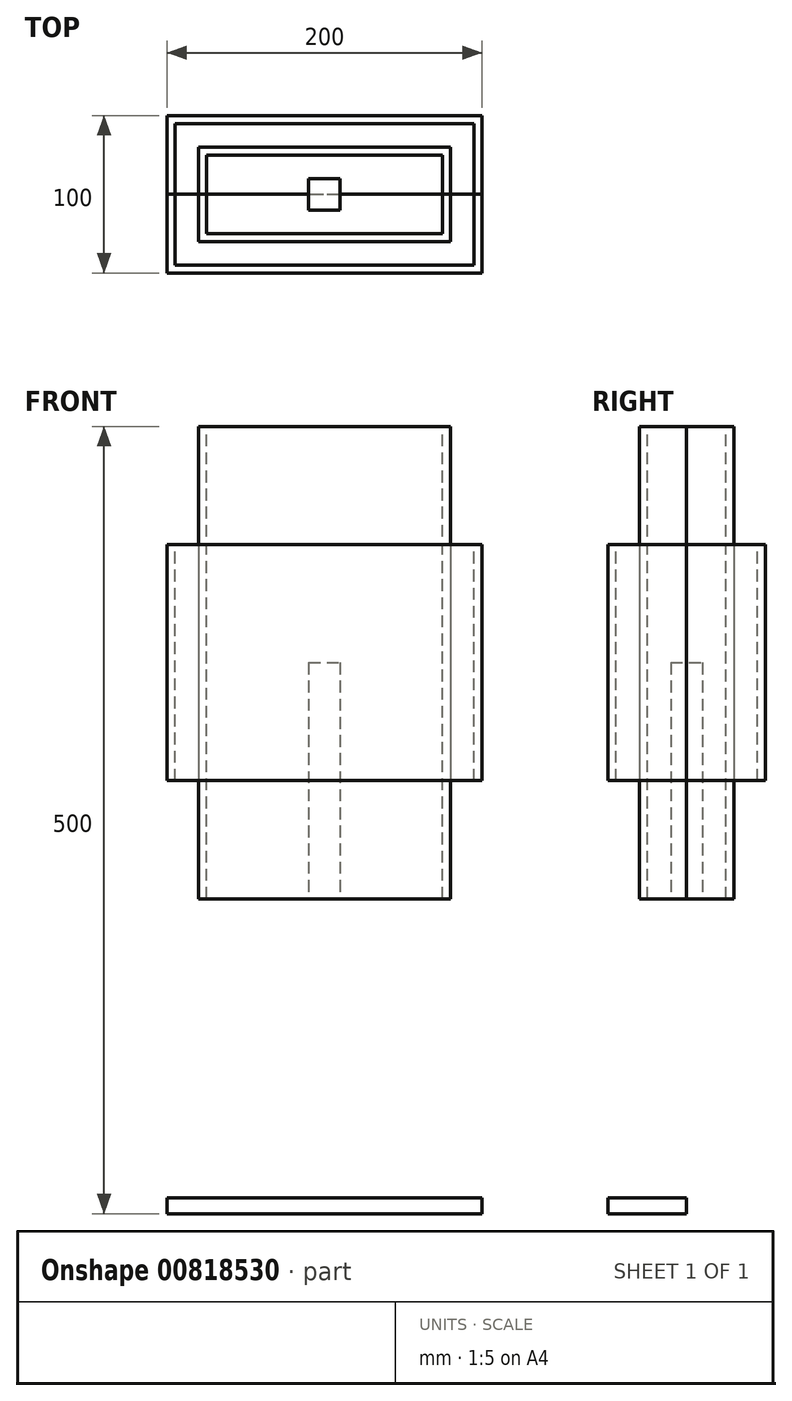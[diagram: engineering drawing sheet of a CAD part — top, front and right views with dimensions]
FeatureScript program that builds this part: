
annotation { "Feature Type Name" : "Feature", "Feature Type Description" : "" }
export const myFeature = defineFeature(function(context is Context, id is Id, definition is map)
    precondition{}
    {
        {
            var Q0;
            Q0=qCreatedBy(makeId("Front.planeOp"),FACE);
            var sketch = newSketch(context, id + "F0", { "sketchPlane" : qUnion([Q0])});
            skLineSegment(sketch, "E0.bottom", {"start": v(-100, 425) * mm, "end": v(100, 425) * mm});
            skLineSegment(sketch, "E0.top", {"start": v(-100, 275) * mm, "end": v(100, 275) * mm});
            skLineSegment(sketch, "E0.left", {"start": v(-100, 425) * mm, "end": v(-100, 275) * mm});
            skLineSegment(sketch, "E0.right", {"start": v(100, 425) * mm, "end": v(100, 275) * mm});
            skLineSegment(sketch, "E1.bottom", {"start": v(-95, 420) * mm, "end": v(95, 420) * mm});
            skLineSegment(sketch, "E1.top", {"start": v(-95, 280) * mm, "end": v(95, 280) * mm});
            skLineSegment(sketch, "E1.left", {"start": v(-95, 420) * mm, "end": v(-95, 280) * mm});
            skLineSegment(sketch, "E1.right", {"start": v(95, 420) * mm, "end": v(95, 280) * mm});
            skLineSegment(sketch, "E2", {"start": v(0, 425) * mm, "end": v(0, 420) * mm});
            skLineSegment(sketch, "E3", {"start": v(-95, 350) * mm, "end": v(-100, 350) * mm, "construction": true});
            skPoint(sketch, "E3.endSnap0", {"position": v(-100, 350) * mm});
            skLineSegment(sketch, "E4.bottom", {"start": v(-100, 10) * mm, "end": v(100, 10) * mm});
            skLineSegment(sketch, "E4.top", {"start": v(-100, 0) * mm, "end": v(100, 0) * mm});
            skLineSegment(sketch, "E4.left", {"start": v(-100, 10) * mm, "end": v(-100, 0) * mm});
            skLineSegment(sketch, "E4.right", {"start": v(100, 10) * mm, "end": v(100, 0) * mm});
            skLineSegment(sketch, "E5.bottom", {"start": v(-10, 350) * mm, "end": v(10, 350) * mm});
            skLineSegment(sketch, "E5.top", {"start": v(-10, 10) * mm, "end": v(10, 10) * mm});
            skLineSegment(sketch, "E5.left", {"start": v(-10, 350) * mm, "end": v(-10, 10) * mm});
            skLineSegment(sketch, "E5.right", {"start": v(10, 350) * mm, "end": v(10, 10) * mm});
            skLineSegment(sketch, "E6", {"start": v(0, 350) * mm, "end": v(0, 10) * mm, "construction": true});
            skLineSegment(sketch, "E7.bottom", {"start": v(-75, 495) * mm, "end": v(75, 495) * mm});
            skLineSegment(sketch, "E7.top", {"start": v(-75, 205) * mm, "end": v(75, 205) * mm});
            skLineSegment(sketch, "E7.left", {"start": v(-75, 495) * mm, "end": v(-75, 205) * mm});
            skLineSegment(sketch, "E7.right", {"start": v(75, 495) * mm, "end": v(75, 205) * mm});
            skLineSegment(sketch, "E8.bottom", {"start": v(-80, 500) * mm, "end": v(80, 500) * mm});
            skLineSegment(sketch, "E8.top", {"start": v(-80, 200) * mm, "end": v(80, 200) * mm});
            skLineSegment(sketch, "E8.left", {"start": v(-80, 500) * mm, "end": v(-80, 200) * mm});
            skLineSegment(sketch, "E8.right", {"start": v(80, 500) * mm, "end": v(80, 200) * mm});
            skLineSegment(sketch, "E9", {"start": v(0, 500) * mm, "end": v(0, 495) * mm, "construction": true});
            skLineSegment(sketch, "E10", {"start": v(-75, 350) * mm, "end": v(-80, 350) * mm, "construction": true});
            skLineSegment(sketch, "E11", {"start": v(0, 495) * mm, "end": v(0, 425) * mm, "construction": true});
            skLineSegment(sketch, "E12", {"start": v(0, 275) * mm, "end": v(0, 205) * mm, "construction": true});
            skLineSegment(sketch, "E13", {"start": v(-75, 350) * mm, "end": v(75, 350) * mm, "construction": true});
            skLineSegment(sketch, "E14", {"start": v(-75, 205) * mm, "end": v(-75, 200) * mm});
            skLineSegment(sketch, "E15", {"start": v(75, 205) * mm, "end": v(75, 200) * mm});
            skLineSegment(sketch, "E16", {"start": v(-95, 280) * mm, "end": v(-95, 275) * mm});
            skLineSegment(sketch, "E17", {"start": v(95, 280) * mm, "end": v(95, 275) * mm});
            skLineSegment(sketch, "E18", {"start": v(-75, 495) * mm, "end": v(-75, 500) * mm});
            skLineSegment(sketch, "E19", {"start": v(75, 495) * mm, "end": v(75, 500) * mm});
            skLineSegment(sketch, "E20", {"start": v(-95, 420) * mm, "end": v(-95, 425) * mm});
            skLineSegment(sketch, "E21", {"start": v(95, 420) * mm, "end": v(95, 425) * mm});
            skSolve(sketch);
        }
        {
            var Q0;
            {var subQ0=sQuery(id+"F0.wireOp",EDGE,"E5.top");Q0=makeQuery(id+"F0.imprint","IMPRINT",FACE,{"disambiguationData":[TD([[makeQuery(id+"F0.imprint","IMPRINT",EDGE,{"derivedFrom":subQ0}),1.0]])]});}
            var Q1;
            {var subQ0=sQuery(id+"F0.wireOp",EDGE,"E8.top");var subQ1=sQuery(id+"F0.wireOp",EDGE,"E5.left");var subQ2=makeQuery(id+"F0.imprint","INTERSECT",VERTEX,{"derivedFrom":[subQ1,subQ0]});Q1=makeQuery(id+"F0.imprint","IMPRINT",FACE,{"disambiguationData":[TD([[makeQuery(id+"F0.imprint","IMPRINT",EDGE,{"disambiguationData":[TD([[subQ2,1.0]])],"derivedFrom":subQ1}),1.0]])]});}
            var Q2;
            {var subQ0=sQuery(id+"F0.wireOp",EDGE,"E5.left");var subQ1=sQuery(id+"F0.wireOp",EDGE,"E0.top");var subQ2=makeQuery(id+"F0.imprint","INTERSECT",VERTEX,{"derivedFrom":[subQ1,subQ0]});Q2=makeQuery(id+"F0.imprint","IMPRINT",FACE,{"disambiguationData":[TD([[makeQuery(id+"F0.imprint","IMPRINT",EDGE,{"disambiguationData":[TD([[subQ2,-1.0]])],"derivedFrom":subQ1}),-1.0]])]});}
            var Q3;
            {var subQ0=sQuery(id+"F0.wireOp",EDGE,"E5.left");var subQ1=sQuery(id+"F0.wireOp",EDGE,"E0.top");var subQ2=makeQuery(id+"F0.imprint","INTERSECT",VERTEX,{"derivedFrom":[subQ1,subQ0]});Q3=makeQuery(id+"F0.imprint","IMPRINT",FACE,{"disambiguationData":[TD([[makeQuery(id+"F0.imprint","IMPRINT",EDGE,{"disambiguationData":[TD([[subQ2,-1.0]])],"derivedFrom":subQ1}),1.0]])]});}
            var Q4;
            {var subQ5=sQuery(id+"F0.wireOp",EDGE,"E5.bottom");Q4=makeQuery(id+"F0.imprint","IMPRINT",FACE,{"disambiguationData":[TD([[makeQuery(id+"F0.imprint","IMPRINT",EDGE,{"derivedFrom":subQ5}),-1.0]])]});}
            extrude(context, id + "F1", {"entities" : qUnion([Q0, Q1, Q2, Q3, Q4]), "depth" : 10 * mm, "offsetDistance" : 25 * mm, "hasSecondDirection" : true, "secondDirectionOppositeDirection" : true, "secondDirectionDepth" : 10 * mm});
        }
        {
            var Q0;
            {var subQ0=sQuery(id+"F0.wireOp",EDGE,"E0.left");Q0=makeQuery(id+"F0.imprint","IMPRINT",FACE,{"disambiguationData":[TD([[makeQuery(id+"F0.imprint","IMPRINT",EDGE,{"derivedFrom":subQ0}),1.0]])]});}
            var Q1;
            {var subQ0=sQuery(id+"F0.wireOp",EDGE,"E0.right");Q1=makeQuery(id+"F0.imprint","IMPRINT",FACE,{"disambiguationData":[TD([[makeQuery(id+"F0.imprint","IMPRINT",EDGE,{"derivedFrom":subQ0}),-1.0]])]});}
            var Q2;
            Q2=makeQuery(id+"F0.imprint","IMPRINT",FACE,{"disambiguationData":[TD([[makeQuery(id+"F0.imprint","IMPRINT",EDGE,{"derivedFrom":sQuery(id+"F0.wireOp",EDGE,"E4.top")}),1.0]])]});
            extrude(context, id + "F2", {"entities" : qUnion([Q0, Q1, Q2]), "operationType" : NewBodyOperationType.ADD, "depth" : 50 * mm, "offsetDistance" : 25 * mm});
        }
        {
            var Q0;
            {var subQ0=sQuery(id+"F0.wireOp",EDGE,"E21");Q0=makeQuery(id+"F0.imprint","IMPRINT",FACE,{"disambiguationData":[TD([[makeQuery(id+"F0.imprint","IMPRINT",EDGE,{"derivedFrom":subQ0}),1.0]])]});}
            var Q1;
            {var subQ0=sQuery(id+"F0.wireOp",EDGE,"E2");Q1=makeQuery(id+"F0.imprint","IMPRINT",FACE,{"disambiguationData":[TD([[makeQuery(id+"F0.imprint","IMPRINT",EDGE,{"derivedFrom":subQ0}),1.0]])]});}
            var Q2;
            {var subQ0=sQuery(id+"F0.wireOp",EDGE,"E8.right");var subQ1=sQuery(id+"F0.wireOp",EDGE,"E0.bottom");var subQ2=makeQuery(id+"F0.imprint","INTERSECT",VERTEX,{"derivedFrom":[subQ1,subQ0]});Q2=makeQuery(id+"F0.imprint","IMPRINT",FACE,{"disambiguationData":[TD([[makeQuery(id+"F0.imprint","IMPRINT",EDGE,{"disambiguationData":[TD([[subQ2,1.0]])],"derivedFrom":subQ1}),-1.0]])]});}
            var Q3;
            {var subQ0=sQuery(id+"F0.wireOp",EDGE,"E2");Q3=makeQuery(id+"F0.imprint","IMPRINT",FACE,{"disambiguationData":[TD([[makeQuery(id+"F0.imprint","IMPRINT",EDGE,{"derivedFrom":subQ0}),-1.0]])]});}
            var Q4;
            {var subQ0=sQuery(id+"F0.wireOp",EDGE,"E20");Q4=makeQuery(id+"F0.imprint","IMPRINT",FACE,{"disambiguationData":[TD([[makeQuery(id+"F0.imprint","IMPRINT",EDGE,{"derivedFrom":subQ0}),-1.0]])]});}
            var Q5;
            {var subQ0=sQuery(id+"F0.wireOp",EDGE,"E8.left");var subQ1=sQuery(id+"F0.wireOp",EDGE,"E0.bottom");var subQ2=makeQuery(id+"F0.imprint","INTERSECT",VERTEX,{"derivedFrom":[subQ1,subQ0]});Q5=makeQuery(id+"F0.imprint","IMPRINT",FACE,{"disambiguationData":[TD([[makeQuery(id+"F0.imprint","IMPRINT",EDGE,{"disambiguationData":[TD([[subQ2,-1.0]])],"derivedFrom":subQ1}),-1.0]])]});}
            var Q6;
            {var subQ0=sQuery(id+"F0.wireOp",EDGE,"E1.left");Q6=makeQuery(id+"F0.imprint","IMPRINT",FACE,{"disambiguationData":[TD([[makeQuery(id+"F0.imprint","IMPRINT",EDGE,{"derivedFrom":subQ0}),1.0]])]});}
            var Q7;
            {var subQ0=sQuery(id+"F0.wireOp",EDGE,"E8.left");var subQ1=sQuery(id+"F0.wireOp",EDGE,"E1.bottom");var subQ2=makeQuery(id+"F0.imprint","INTERSECT",VERTEX,{"derivedFrom":[subQ1,subQ0]});Q7=makeQuery(id+"F0.imprint","IMPRINT",FACE,{"disambiguationData":[TD([[makeQuery(id+"F0.imprint","IMPRINT",EDGE,{"disambiguationData":[TD([[subQ2,-1.0]])],"derivedFrom":subQ1}),-1.0]])]});}
            var Q8;
            {var subQ0=sQuery(id+"F0.wireOp",EDGE,"E7.right");var subQ1=sQuery(id+"F0.wireOp",EDGE,"E1.bottom");var subQ2=makeQuery(id+"F0.imprint","INTERSECT",VERTEX,{"derivedFrom":[subQ1,subQ0]});Q8=makeQuery(id+"F0.imprint","IMPRINT",FACE,{"disambiguationData":[TD([[makeQuery(id+"F0.imprint","IMPRINT",EDGE,{"disambiguationData":[TD([[subQ2,-1.0]])],"derivedFrom":subQ1}),-1.0]])]});}
            var Q9;
            {var subQ0=sQuery(id+"F0.wireOp",EDGE,"E1.right");Q9=makeQuery(id+"F0.imprint","IMPRINT",FACE,{"disambiguationData":[TD([[makeQuery(id+"F0.imprint","IMPRINT",EDGE,{"derivedFrom":subQ0}),-1.0]])]});}
            var Q10;
            {var subQ5=sQuery(id+"F0.wireOp",EDGE,"E5.bottom");Q10=makeQuery(id+"F0.imprint","IMPRINT",FACE,{"disambiguationData":[TD([[makeQuery(id+"F0.imprint","IMPRINT",EDGE,{"derivedFrom":subQ5}),1.0]])]});}
            var Q11;
            {var subQ5=sQuery(id+"F0.wireOp",EDGE,"E5.bottom");Q11=makeQuery(id+"F0.imprint","IMPRINT",FACE,{"disambiguationData":[TD([[makeQuery(id+"F0.imprint","IMPRINT",EDGE,{"derivedFrom":subQ5}),-1.0]])]});}
            var Q12;
            {var subQ0=sQuery(id+"F0.wireOp",EDGE,"E17");Q12=makeQuery(id+"F0.imprint","IMPRINT",FACE,{"disambiguationData":[TD([[makeQuery(id+"F0.imprint","IMPRINT",EDGE,{"derivedFrom":subQ0}),-1.0]])]});}
            var Q13;
            {var subQ0=sQuery(id+"F0.wireOp",EDGE,"E8.right");var subQ1=sQuery(id+"F0.wireOp",EDGE,"E0.top");var subQ2=makeQuery(id+"F0.imprint","INTERSECT",VERTEX,{"derivedFrom":[subQ1,subQ0]});Q13=makeQuery(id+"F0.imprint","IMPRINT",FACE,{"disambiguationData":[TD([[makeQuery(id+"F0.imprint","IMPRINT",EDGE,{"disambiguationData":[TD([[subQ2,1.0]])],"derivedFrom":subQ1}),1.0]])]});}
            var Q14;
            {var subQ0=sQuery(id+"F0.wireOp",EDGE,"E5.right");var subQ1=sQuery(id+"F0.wireOp",EDGE,"E0.top");var subQ2=makeQuery(id+"F0.imprint","INTERSECT",VERTEX,{"derivedFrom":[subQ1,subQ0]});Q14=makeQuery(id+"F0.imprint","IMPRINT",FACE,{"disambiguationData":[TD([[makeQuery(id+"F0.imprint","IMPRINT",EDGE,{"disambiguationData":[TD([[subQ2,-1.0]])],"derivedFrom":subQ1}),1.0]])]});}
            var Q15;
            {var subQ0=sQuery(id+"F0.wireOp",EDGE,"E5.left");var subQ1=sQuery(id+"F0.wireOp",EDGE,"E0.top");var subQ2=makeQuery(id+"F0.imprint","INTERSECT",VERTEX,{"derivedFrom":[subQ1,subQ0]});Q15=makeQuery(id+"F0.imprint","IMPRINT",FACE,{"disambiguationData":[TD([[makeQuery(id+"F0.imprint","IMPRINT",EDGE,{"disambiguationData":[TD([[subQ2,-1.0]])],"derivedFrom":subQ1}),1.0]])]});}
            var Q16;
            {var subQ0=sQuery(id+"F0.wireOp",EDGE,"E7.left");var subQ1=sQuery(id+"F0.wireOp",EDGE,"E0.top");var subQ2=makeQuery(id+"F0.imprint","INTERSECT",VERTEX,{"derivedFrom":[subQ1,subQ0]});Q16=makeQuery(id+"F0.imprint","IMPRINT",FACE,{"disambiguationData":[TD([[makeQuery(id+"F0.imprint","IMPRINT",EDGE,{"disambiguationData":[TD([[subQ2,-1.0]])],"derivedFrom":subQ1}),1.0]])]});}
            var Q17;
            {var subQ0=sQuery(id+"F0.wireOp",EDGE,"E8.left");var subQ1=sQuery(id+"F0.wireOp",EDGE,"E0.top");var subQ2=makeQuery(id+"F0.imprint","INTERSECT",VERTEX,{"derivedFrom":[subQ1,subQ0]});Q17=makeQuery(id+"F0.imprint","IMPRINT",FACE,{"disambiguationData":[TD([[makeQuery(id+"F0.imprint","IMPRINT",EDGE,{"disambiguationData":[TD([[subQ2,-1.0]])],"derivedFrom":subQ1}),1.0]])]});}
            var Q18;
            {var subQ0=sQuery(id+"F0.wireOp",EDGE,"E16");Q18=makeQuery(id+"F0.imprint","IMPRINT",FACE,{"disambiguationData":[TD([[makeQuery(id+"F0.imprint","IMPRINT",EDGE,{"derivedFrom":subQ0}),1.0]])]});}
            extrude(context, id + "F3", {"entities" : qUnion([Q0, Q1, Q2, Q3, Q4, Q5, Q6, Q7, Q8, Q9, Q10, Q11, Q12, Q13, Q14, Q15, Q16, Q17, Q18]), "operationType" : NewBodyOperationType.ADD, "depth" : 50 * mm, "offsetDistance" : 25 * mm, "hasSecondDirection" : true, "secondDirectionOppositeDirection" : false, "secondDirectionDepth" : 45 * mm});
        }
        {
            var Q0;
            {var subQ5=sQuery(id+"F0.wireOp",EDGE,"E19");Q0=makeQuery(id+"F0.imprint","IMPRINT",FACE,{"disambiguationData":[TD([[makeQuery(id+"F0.imprint","IMPRINT",EDGE,{"derivedFrom":subQ5}),-1.0]])]});}
            var Q1;
            {var subQ0=sQuery(id+"F0.wireOp",EDGE,"E8.right");var subQ1=sQuery(id+"F0.wireOp",EDGE,"E0.bottom");var subQ2=makeQuery(id+"F0.imprint","INTERSECT",VERTEX,{"derivedFrom":[subQ1,subQ0]});Q1=makeQuery(id+"F0.imprint","IMPRINT",FACE,{"disambiguationData":[TD([[makeQuery(id+"F0.imprint","IMPRINT",EDGE,{"disambiguationData":[TD([[subQ2,1.0]])],"derivedFrom":subQ1}),-1.0]])]});}
            var Q2;
            {var subQ0=sQuery(id+"F0.wireOp",EDGE,"E7.right");var subQ1=sQuery(id+"F0.wireOp",EDGE,"E1.bottom");var subQ2=makeQuery(id+"F0.imprint","INTERSECT",VERTEX,{"derivedFrom":[subQ1,subQ0]});Q2=makeQuery(id+"F0.imprint","IMPRINT",FACE,{"disambiguationData":[TD([[makeQuery(id+"F0.imprint","IMPRINT",EDGE,{"disambiguationData":[TD([[subQ2,-1.0]])],"derivedFrom":subQ1}),-1.0]])]});}
            var Q3;
            {var subQ0=sQuery(id+"F0.wireOp",EDGE,"E8.right");var subQ1=sQuery(id+"F0.wireOp",EDGE,"E0.top");var subQ2=makeQuery(id+"F0.imprint","INTERSECT",VERTEX,{"derivedFrom":[subQ1,subQ0]});Q3=makeQuery(id+"F0.imprint","IMPRINT",FACE,{"disambiguationData":[TD([[makeQuery(id+"F0.imprint","IMPRINT",EDGE,{"disambiguationData":[TD([[subQ2,1.0]])],"derivedFrom":subQ1}),1.0]])]});}
            var Q4;
            {var subQ5=sQuery(id+"F0.wireOp",EDGE,"E15");Q4=makeQuery(id+"F0.imprint","IMPRINT",FACE,{"disambiguationData":[TD([[makeQuery(id+"F0.imprint","IMPRINT",EDGE,{"derivedFrom":subQ5}),1.0]])]});}
            var Q5;
            {var subQ5=sQuery(id+"F0.wireOp",EDGE,"E14");Q5=makeQuery(id+"F0.imprint","IMPRINT",FACE,{"disambiguationData":[TD([[makeQuery(id+"F0.imprint","IMPRINT",EDGE,{"derivedFrom":subQ5}),-1.0]])]});}
            var Q6;
            {var subQ0=sQuery(id+"F0.wireOp",EDGE,"E8.left");var subQ1=sQuery(id+"F0.wireOp",EDGE,"E0.top");var subQ2=makeQuery(id+"F0.imprint","INTERSECT",VERTEX,{"derivedFrom":[subQ1,subQ0]});Q6=makeQuery(id+"F0.imprint","IMPRINT",FACE,{"disambiguationData":[TD([[makeQuery(id+"F0.imprint","IMPRINT",EDGE,{"disambiguationData":[TD([[subQ2,-1.0]])],"derivedFrom":subQ1}),1.0]])]});}
            var Q7;
            {var subQ0=sQuery(id+"F0.wireOp",EDGE,"E8.left");var subQ1=sQuery(id+"F0.wireOp",EDGE,"E1.bottom");var subQ2=makeQuery(id+"F0.imprint","INTERSECT",VERTEX,{"derivedFrom":[subQ1,subQ0]});Q7=makeQuery(id+"F0.imprint","IMPRINT",FACE,{"disambiguationData":[TD([[makeQuery(id+"F0.imprint","IMPRINT",EDGE,{"disambiguationData":[TD([[subQ2,-1.0]])],"derivedFrom":subQ1}),-1.0]])]});}
            var Q8;
            {var subQ5=sQuery(id+"F0.wireOp",EDGE,"E18");Q8=makeQuery(id+"F0.imprint","IMPRINT",FACE,{"disambiguationData":[TD([[makeQuery(id+"F0.imprint","IMPRINT",EDGE,{"derivedFrom":subQ5}),1.0]])]});}
            var Q9;
            {var subQ0=sQuery(id+"F0.wireOp",EDGE,"E8.left");var subQ1=sQuery(id+"F0.wireOp",EDGE,"E0.bottom");var subQ2=makeQuery(id+"F0.imprint","INTERSECT",VERTEX,{"derivedFrom":[subQ1,subQ0]});Q9=makeQuery(id+"F0.imprint","IMPRINT",FACE,{"disambiguationData":[TD([[makeQuery(id+"F0.imprint","IMPRINT",EDGE,{"disambiguationData":[TD([[subQ2,-1.0]])],"derivedFrom":subQ1}),-1.0]])]});}
            extrude(context, id + "F4", {"entities" : qUnion([Q0, Q1, Q2, Q3, Q4, Q5, Q6, Q7, Q8, Q9]), "depth" : 30 * mm, "offsetDistance" : 25 * mm});
        }
        {
            var Q0;
            Q0=makeQuery(id+"F0.imprint","IMPRINT",FACE,{"disambiguationData":[TD([[makeQuery(id+"F0.imprint","IMPRINT",EDGE,{"derivedFrom":sQuery(id+"F0.wireOp",EDGE,"E7.bottom")}),1.0]])]});
            var Q1;
            {var subQ1=sQuery(id+"F0.wireOp",EDGE,"E7.bottom");Q1=makeQuery(id+"F0.imprint","IMPRINT",FACE,{"disambiguationData":[TD([[makeQuery(id+"F0.imprint","IMPRINT",EDGE,{"derivedFrom":subQ1}),-1.0]])]});}
            var Q2;
            {var subQ0=sQuery(id+"F0.wireOp",EDGE,"E2");Q2=makeQuery(id+"F0.imprint","IMPRINT",FACE,{"disambiguationData":[TD([[makeQuery(id+"F0.imprint","IMPRINT",EDGE,{"derivedFrom":subQ0}),1.0]])]});}
            var Q3;
            {var subQ0=sQuery(id+"F0.wireOp",EDGE,"E2");Q3=makeQuery(id+"F0.imprint","IMPRINT",FACE,{"disambiguationData":[TD([[makeQuery(id+"F0.imprint","IMPRINT",EDGE,{"derivedFrom":subQ0}),-1.0]])]});}
            var Q4;
            {var subQ5=sQuery(id+"F0.wireOp",EDGE,"E5.bottom");Q4=makeQuery(id+"F0.imprint","IMPRINT",FACE,{"disambiguationData":[TD([[makeQuery(id+"F0.imprint","IMPRINT",EDGE,{"derivedFrom":subQ5}),1.0]])]});}
            var Q5;
            {var subQ5=sQuery(id+"F0.wireOp",EDGE,"E5.bottom");Q5=makeQuery(id+"F0.imprint","IMPRINT",FACE,{"disambiguationData":[TD([[makeQuery(id+"F0.imprint","IMPRINT",EDGE,{"derivedFrom":subQ5}),-1.0]])]});}
            var Q6;
            {var subQ0=sQuery(id+"F0.wireOp",EDGE,"E5.left");var subQ1=sQuery(id+"F0.wireOp",EDGE,"E0.top");var subQ2=makeQuery(id+"F0.imprint","INTERSECT",VERTEX,{"derivedFrom":[subQ1,subQ0]});Q6=makeQuery(id+"F0.imprint","IMPRINT",FACE,{"disambiguationData":[TD([[makeQuery(id+"F0.imprint","IMPRINT",EDGE,{"disambiguationData":[TD([[subQ2,-1.0]])],"derivedFrom":subQ1}),1.0]])]});}
            var Q7;
            {var subQ0=sQuery(id+"F0.wireOp",EDGE,"E7.left");var subQ1=sQuery(id+"F0.wireOp",EDGE,"E0.top");var subQ2=makeQuery(id+"F0.imprint","INTERSECT",VERTEX,{"derivedFrom":[subQ1,subQ0]});Q7=makeQuery(id+"F0.imprint","IMPRINT",FACE,{"disambiguationData":[TD([[makeQuery(id+"F0.imprint","IMPRINT",EDGE,{"disambiguationData":[TD([[subQ2,-1.0]])],"derivedFrom":subQ1}),1.0]])]});}
            var Q8;
            {var subQ0=sQuery(id+"F0.wireOp",EDGE,"E5.right");var subQ1=sQuery(id+"F0.wireOp",EDGE,"E0.top");var subQ2=makeQuery(id+"F0.imprint","INTERSECT",VERTEX,{"derivedFrom":[subQ1,subQ0]});Q8=makeQuery(id+"F0.imprint","IMPRINT",FACE,{"disambiguationData":[TD([[makeQuery(id+"F0.imprint","IMPRINT",EDGE,{"disambiguationData":[TD([[subQ2,-1.0]])],"derivedFrom":subQ1}),1.0]])]});}
            var Q9;
            {var subQ0=sQuery(id+"F0.wireOp",EDGE,"E5.right");var subQ1=sQuery(id+"F0.wireOp",EDGE,"E0.top");var subQ2=makeQuery(id+"F0.imprint","INTERSECT",VERTEX,{"derivedFrom":[subQ1,subQ0]});Q9=makeQuery(id+"F0.imprint","IMPRINT",FACE,{"disambiguationData":[TD([[makeQuery(id+"F0.imprint","IMPRINT",EDGE,{"disambiguationData":[TD([[subQ2,-1.0]])],"derivedFrom":subQ1}),-1.0]])]});}
            var Q10;
            {var subQ0=sQuery(id+"F0.wireOp",EDGE,"E7.left");var subQ1=sQuery(id+"F0.wireOp",EDGE,"E0.top");var subQ2=makeQuery(id+"F0.imprint","INTERSECT",VERTEX,{"derivedFrom":[subQ1,subQ0]});Q10=makeQuery(id+"F0.imprint","IMPRINT",FACE,{"disambiguationData":[TD([[makeQuery(id+"F0.imprint","IMPRINT",EDGE,{"disambiguationData":[TD([[subQ2,-1.0]])],"derivedFrom":subQ1}),-1.0]])]});}
            var Q11;
            {var subQ0=sQuery(id+"F0.wireOp",EDGE,"E5.left");var subQ1=sQuery(id+"F0.wireOp",EDGE,"E0.top");var subQ2=makeQuery(id+"F0.imprint","INTERSECT",VERTEX,{"derivedFrom":[subQ1,subQ0]});Q11=makeQuery(id+"F0.imprint","IMPRINT",FACE,{"disambiguationData":[TD([[makeQuery(id+"F0.imprint","IMPRINT",EDGE,{"disambiguationData":[TD([[subQ2,-1.0]])],"derivedFrom":subQ1}),-1.0]])]});}
            var Q12;
            {var subQ5=sQuery(id+"F0.wireOp",EDGE,"E15");Q12=makeQuery(id+"F0.imprint","IMPRINT",FACE,{"disambiguationData":[TD([[makeQuery(id+"F0.imprint","IMPRINT",EDGE,{"derivedFrom":subQ5}),-1.0]])]});}
            var Q13;
            {var subQ0=sQuery(id+"F0.wireOp",EDGE,"E8.top");var subQ1=sQuery(id+"F0.wireOp",EDGE,"E5.left");var subQ2=makeQuery(id+"F0.imprint","INTERSECT",VERTEX,{"derivedFrom":[subQ1,subQ0]});Q13=makeQuery(id+"F0.imprint","IMPRINT",FACE,{"disambiguationData":[TD([[makeQuery(id+"F0.imprint","IMPRINT",EDGE,{"disambiguationData":[TD([[subQ2,1.0]])],"derivedFrom":subQ1}),1.0]])]});}
            var Q14;
            {var subQ5=sQuery(id+"F0.wireOp",EDGE,"E14");Q14=makeQuery(id+"F0.imprint","IMPRINT",FACE,{"disambiguationData":[TD([[makeQuery(id+"F0.imprint","IMPRINT",EDGE,{"derivedFrom":subQ5}),1.0]])]});}
            extrude(context, id + "F5", {"entities" : qUnion([Q0, Q1, Q2, Q3, Q4, Q5, Q6, Q7, Q8, Q9, Q10, Q11, Q12, Q13, Q14]), "operationType" : NewBodyOperationType.ADD, "depth" : 30 * mm, "offsetDistance" : 25 * mm, "hasSecondDirection" : true, "secondDirectionOppositeDirection" : false, "secondDirectionDepth" : 25 * mm});
        }
        {
            var Q0;
            Q0=makeQuery(id+"F4.opExtrude","SWEPT_BODY",BODY,{"disambiguationData":[OSD([sQuery(id+"F0.wireOp",EDGE,"E7.left"),sQuery(id+"F0.wireOp",EDGE,"E8.bottom"),sQuery(id+"F0.wireOp",EDGE,"E8.top"),sQuery(id+"F0.wireOp",EDGE,"E8.left"),sQuery(id+"F0.wireOp",EDGE,"E14"),sQuery(id+"F0.wireOp",EDGE,"E18")])]});
            var Q1;
            Q1=makeQuery(id+"F2.opExtrude","SWEPT_BODY",BODY,{"disambiguationData":[OSD([sQuery(id+"F0.wireOp",EDGE,"E0.bottom"),sQuery(id+"F0.wireOp",EDGE,"E0.top"),sQuery(id+"F0.wireOp",EDGE,"E0.left"),sQuery(id+"F0.wireOp",EDGE,"E1.left"),sQuery(id+"F0.wireOp",EDGE,"E16"),sQuery(id+"F0.wireOp",EDGE,"E20")])]});
            var Q2;
            Q2=makeQuery(id+"F1.opExtrude","SWEPT_BODY",BODY,{"disambiguationData":[OSD([sQuery(id+"F0.wireOp",EDGE,"E5.bottom"),sQuery(id+"F0.wireOp",EDGE,"E5.top"),sQuery(id+"F0.wireOp",EDGE,"E5.left"),sQuery(id+"F0.wireOp",EDGE,"E5.right")])]});
            var Q3;
            Q3=qCreatedBy(makeId("Front.planeOp"),FACE);
            mirror(context, id + "F6", {"operationType" : NewBodyOperationType.ADD, "entities" : qUnion([Q0, Q1, Q2]), "mirrorPlane" : qUnion([Q3])});
        }
    });
